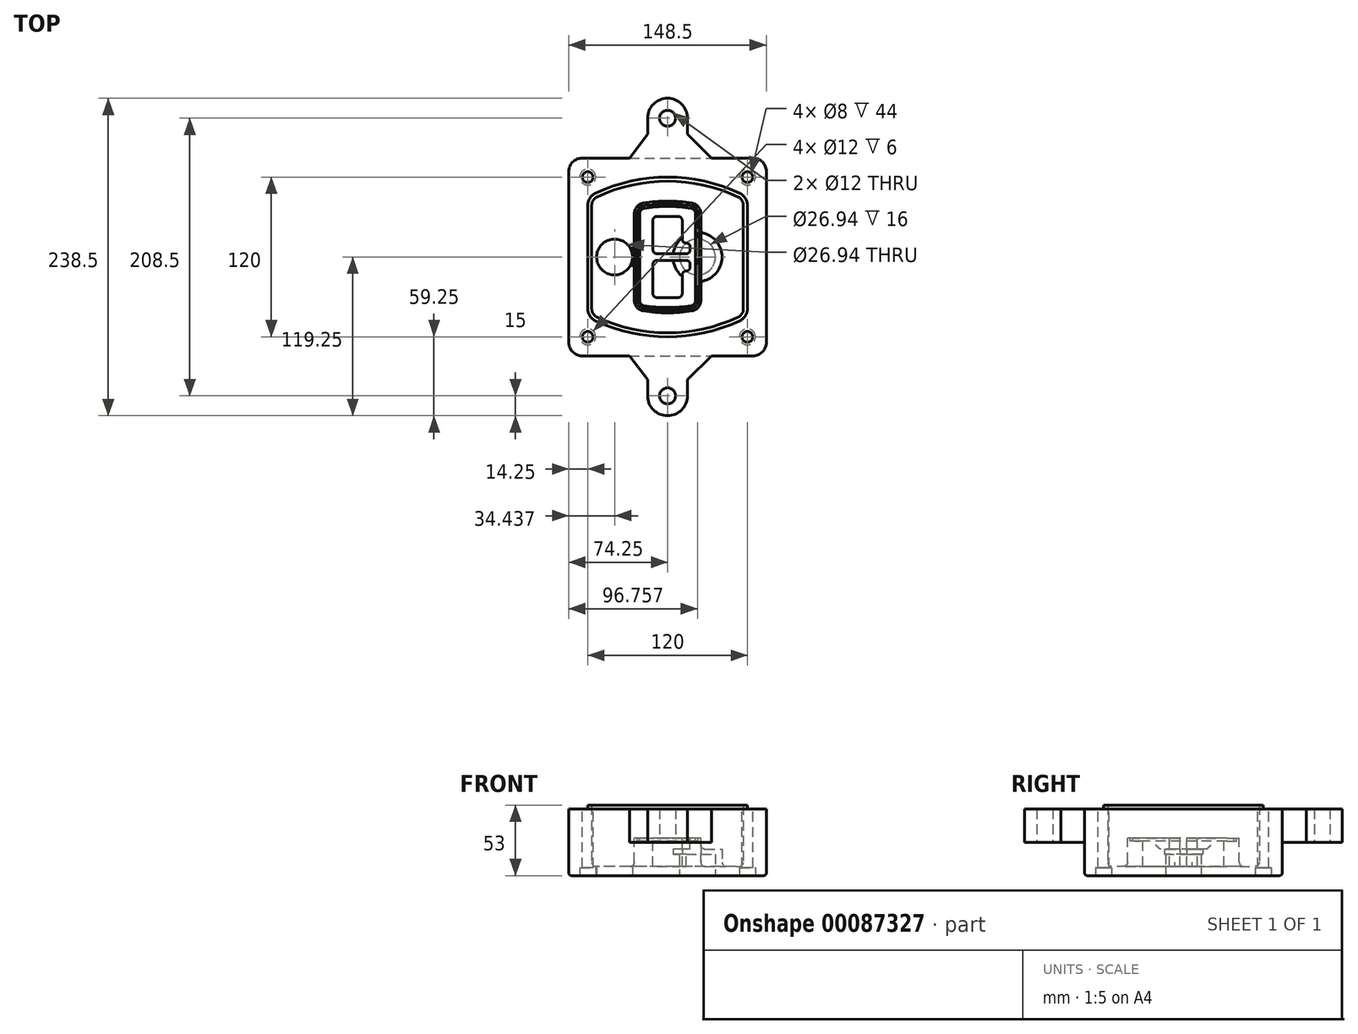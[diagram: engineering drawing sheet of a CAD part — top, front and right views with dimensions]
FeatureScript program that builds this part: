
annotation { "Feature Type Name" : "Feature", "Feature Type Description" : "" }
export const myFeature = defineFeature(function(context is Context, id is Id, definition is map)
    precondition{}
    {
        {
            var Q0;
            Q0=qCreatedBy(makeId("Top.planeOp"),FACE);
            var sketch = newSketch(context, id + "F0", { "sketchPlane" : qUnion([Q0])});
            skPoint(sketch, "E0.rect.middle", {"position": v(0, 0) * mm});
            skLineSegment(sketch, "E1.bottom", {"start": v(-64.25, -74.25) * mm, "end": v(64.25, -74.25) * mm});
            skLineSegment(sketch, "E1.top", {"start": v(-64.25, 74.25) * mm, "end": v(64.25, 74.25) * mm});
            skLineSegment(sketch, "E1.left", {"start": v(-74.25, -64.25) * mm, "end": v(-74.25, 64.25) * mm});
            skLineSegment(sketch, "E1.right", {"start": v(74.25, -64.25) * mm, "end": v(74.25, 64.25) * mm});
            skLineSegment(sketch, "E2", {"start": v(-74.25, 74.25) * mm, "end": v(74.25, -74.25) * mm, "construction": true});
            skLineSegment(sketch, "E3", {"start": v(74.25, 74.25) * mm, "end": v(-74.25, -74.25) * mm, "construction": true});
            skCircle(sketch, "E4", {"center": v(-60, 60) * mm, "radius": 4 * mm});
            skCircle(sketch, "E5", {"center": v(60, 60) * mm, "radius": 4 * mm});
            skCircle(sketch, "E6", {"center": v(60, -60) * mm, "radius": 4 * mm});
            skCircle(sketch, "E7", {"center": v(-60, -60) * mm, "radius": 4 * mm});
            skLineSegment(sketch, "E8", {"start": v(-60, 60) * mm, "end": v(60, 60) * mm, "construction": true});
            skLineSegment(sketch, "E9", {"start": v(60, 60) * mm, "end": v(60, -60) * mm, "construction": true});
            skLineSegment(sketch, "E10", {"start": v(60, -60) * mm, "end": v(-60, -60) * mm, "construction": true});
            skLineSegment(sketch, "E11", {"start": v(-60, -60) * mm, "end": v(-60, 60) * mm, "construction": true});
            skLineSegment(sketch, "E12", {"start": v(-60, 38.83) * mm, "end": v(-60, -38.83) * mm});
            skLineSegment(sketch, "E13", {"start": v(60, 38.83) * mm, "end": v(60, -38.83) * mm});
            skArc(sketch, "E14", {"start": v(54.26, 47.88) * mm, "mid": v(0, 60) * mm, "end": v(-54.26, 47.88) * mm});
            skArc(sketch, "E15", {"start": v(-54.26, -47.88) * mm, "mid": v(0, -60) * mm, "end": v(54.26, -47.88) * mm});
            skLineSegment(sketch, "E16", {"start": v(-60, 0) * mm, "end": v(60, 0) * mm, "construction": true});
            skPoint(sketch, "E17.visualSharp", {"position": v(-60, -45) * mm});
            skArc(sketch, "E17.filletArc", {"start": v(-60, -38.83) * mm, "mid": v(-58.44, -44.2) * mm, "end": v(-54.26, -47.88) * mm});
            skPoint(sketch, "E18.visualSharp", {"position": v(-60, 45) * mm});
            skArc(sketch, "E18.filletArc", {"start": v(-54.26, 47.88) * mm, "mid": v(-58.44, 44.2) * mm, "end": v(-60, 38.83) * mm});
            skPoint(sketch, "E19.visualSharp", {"position": v(60, 45) * mm});
            skArc(sketch, "E19.filletArc", {"start": v(60, 38.83) * mm, "mid": v(58.44, 44.2) * mm, "end": v(54.26, 47.88) * mm});
            skPoint(sketch, "E20.visualSharp", {"position": v(60, -45) * mm});
            skArc(sketch, "E20.filletArc", {"start": v(54.26, -47.88) * mm, "mid": v(58.44, -44.2) * mm, "end": v(60, -38.83) * mm});
            skPoint(sketch, "E21.visualSharp", {"position": v(-74.25, 74.25) * mm});
            skArc(sketch, "E21.filletArc", {"start": v(-64.25, 74.25) * mm, "mid": v(-71.32, 71.32) * mm, "end": v(-74.25, 64.25) * mm});
            skPoint(sketch, "E22.visualSharp", {"position": v(74.25, 74.25) * mm});
            skArc(sketch, "E22.filletArc", {"start": v(74.25, 64.25) * mm, "mid": v(71.32, 71.32) * mm, "end": v(64.25, 74.25) * mm});
            skPoint(sketch, "E23.visualSharp", {"position": v(74.25, -74.25) * mm});
            skArc(sketch, "E23.filletArc", {"start": v(64.25, -74.25) * mm, "mid": v(71.32, -71.32) * mm, "end": v(74.25, -64.25) * mm});
            skPoint(sketch, "E24.visualSharp", {"position": v(-74.25, -74.25) * mm});
            skArc(sketch, "E24.filletArc", {"start": v(-74.25, -64.25) * mm, "mid": v(-71.32, -71.32) * mm, "end": v(-64.25, -74.25) * mm});
            skArc(sketch, "E25.0", {"start": v(57, 38.83) * mm, "mid": v(55.9, 42.58) * mm, "end": v(52.98, 45.17) * mm});
            skLineSegment(sketch, "E25.1", {"start": v(57, 38.83) * mm, "end": v(57, -38.83) * mm});
            skArc(sketch, "E25.2", {"start": v(52.98, -45.17) * mm, "mid": v(55.9, -42.58) * mm, "end": v(57, -38.83) * mm});
            skArc(sketch, "E25.3", {"start": v(-52.98, -45.17) * mm, "mid": v(0, -57) * mm, "end": v(52.98, -45.17) * mm});
            skArc(sketch, "E25.4", {"start": v(-57, -38.83) * mm, "mid": v(-55.9, -42.58) * mm, "end": v(-52.98, -45.17) * mm});
            skArc(sketch, "E25.5", {"start": v(52.98, 45.17) * mm, "mid": v(0, 57) * mm, "end": v(-52.98, 45.17) * mm});
            skLineSegment(sketch, "E25.6", {"start": v(-57, 38.83) * mm, "end": v(-57, -38.83) * mm});
            skArc(sketch, "E25.7", {"start": v(-52.98, 45.17) * mm, "mid": v(-55.9, 42.58) * mm, "end": v(-57, 38.83) * mm});
            skArc(sketch, "E26.0", {"start": v(-55.96, 51.5) * mm, "mid": v(-61.82, 46.33) * mm, "end": v(-64, 38.83) * mm});
            skArc(sketch, "E26.1", {"start": v(55.96, 51.5) * mm, "mid": v(0, 64) * mm, "end": v(-55.96, 51.5) * mm});
            skArc(sketch, "E26.2", {"start": v(64, 38.83) * mm, "mid": v(61.82, 46.33) * mm, "end": v(55.96, 51.5) * mm});
            skLineSegment(sketch, "E26.3", {"start": v(64, 38.83) * mm, "end": v(64, -38.83) * mm});
            skArc(sketch, "E26.4", {"start": v(55.96, -51.5) * mm, "mid": v(61.82, -46.33) * mm, "end": v(64, -38.83) * mm});
            skLineSegment(sketch, "E26.5", {"start": v(-64, 38.83) * mm, "end": v(-64, -38.83) * mm});
            skArc(sketch, "E26.6", {"start": v(-55.96, -51.5) * mm, "mid": v(0, -64) * mm, "end": v(55.96, -51.5) * mm});
            skArc(sketch, "E26.7", {"start": v(-64, -38.83) * mm, "mid": v(-61.82, -46.33) * mm, "end": v(-55.96, -51.5) * mm});
            skSolve(sketch);
        }
        {
            var Q0;
            Q0=makeQuery(id+"F0.imprint","IMPRINT",FACE,{"disambiguationData":[TD([[makeQuery(id+"F0.imprint","IMPRINT",EDGE,{"derivedFrom":sQuery(id+"F0.wireOp",EDGE,"E1.bottom")}),1.0]])]});
            var Q1;
            Q1=makeQuery(id+"F0.imprint","IMPRINT",FACE,{"disambiguationData":[TD([[makeQuery(id+"F0.imprint","IMPRINT",EDGE,{"derivedFrom":sQuery(id+"F0.wireOp",EDGE,"E12")}),1.0]])]});
            var Q2;
            Q2=makeQuery(id+"F0.imprint","IMPRINT",FACE,{"disambiguationData":[TD([[makeQuery(id+"F0.imprint","IMPRINT",EDGE,{"derivedFrom":sQuery(id+"F0.wireOp",EDGE,"E25.0")}),1.0]])]});
            var Q3;
            Q3=makeQuery(id+"F0.imprint","IMPRINT",FACE,{"disambiguationData":[TD([[makeQuery(id+"F0.imprint","IMPRINT",EDGE,{"derivedFrom":sQuery(id+"F0.wireOp",EDGE,"E12")}),-1.0]])]});
            extrude(context, id + "F1", {"entities" : qUnion([Q0, Q1, Q2, Q3]), "oppositeDirection" : true, "depth" : 25 * mm});
        }
        {
            var Q0;
            Q0=makeQuery(id+"F0.imprint","IMPRINT",FACE,{"disambiguationData":[TD([[makeQuery(id+"F0.imprint","IMPRINT",EDGE,{"derivedFrom":sQuery(id+"F0.wireOp",EDGE,"E12")}),1.0]])]});
            extrude(context, id + "F2", {"entities" : qUnion([Q0]), "operationType" : NewBodyOperationType.ADD, "depth" : 3 * mm});
        }
        {
            var Q0;
            Q0=makeQuery(id+"F0.imprint","IMPRINT",FACE,{"disambiguationData":[TD([[makeQuery(id+"F0.imprint","IMPRINT",EDGE,{"derivedFrom":sQuery(id+"F0.wireOp",EDGE,"E25.0")}),1.0]])]});
            extrude(context, id + "F3", {"entities" : qUnion([Q0]), "operationType" : NewBodyOperationType.REMOVE, "oppositeDirection" : true, "depth" : 18 * mm});
        }
        {
            var Q0;
            Q0=makeQuery(id+"F2.opExtrude","CAP_FACE",FACE,{"disambiguationData":[OSD([sQuery(id+"F0.wireOp",EDGE,"E12"),sQuery(id+"F0.wireOp",EDGE,"E13"),sQuery(id+"F0.wireOp",EDGE,"E14"),sQuery(id+"F0.wireOp",EDGE,"E15"),sQuery(id+"F0.wireOp",EDGE,"E17.filletArc"),sQuery(id+"F0.wireOp",EDGE,"E18.filletArc"),sQuery(id+"F0.wireOp",EDGE,"E19.filletArc"),sQuery(id+"F0.wireOp",EDGE,"E20.filletArc"),sQuery(id+"F0.wireOp",EDGE,"E25.0"),sQuery(id+"F0.wireOp",EDGE,"E25.1"),sQuery(id+"F0.wireOp",EDGE,"E25.2"),sQuery(id+"F0.wireOp",EDGE,"E25.3"),sQuery(id+"F0.wireOp",EDGE,"E25.4"),sQuery(id+"F0.wireOp",EDGE,"E25.5"),sQuery(id+"F0.wireOp",EDGE,"E25.6"),sQuery(id+"F0.wireOp",EDGE,"E25.7")])],"isStart":false});
            var sketch = newSketch(context, id + "F4", { "sketchPlane" : qUnion([Q0])});
            skArc(sketch, "E27.0", {"start": v(-18.34, -40.45) * mm, "mid": v(0, -42) * mm, "end": v(18.34, -40.45) * mm});
            skArc(sketch, "E28.0", {"start": v(18.34, 40.45) * mm, "mid": v(0, 42) * mm, "end": v(-18.34, 40.45) * mm});
            skLineSegment(sketch, "E29", {"start": v(-25, 32.57) * mm, "end": v(-25, -32.57) * mm});
            skLineSegment(sketch, "E30", {"start": v(25, 32.57) * mm, "end": v(25, -32.57) * mm});
            skLineSegment(sketch, "E31", {"start": v(-25, 39.1) * mm, "end": v(25, 39.1) * mm, "construction": true});
            skLineSegment(sketch, "E32", {"start": v(-25, -39.1) * mm, "end": v(25, -39.1) * mm, "construction": true});
            skPoint(sketch, "E33.visualSharp", {"position": v(-25, 39.1) * mm});
            skArc(sketch, "E33.filletArc", {"start": v(-18.34, 40.45) * mm, "mid": v(-23.11, 37.73) * mm, "end": v(-25, 32.57) * mm});
            skPoint(sketch, "E34.visualSharp", {"position": v(25, 39.1) * mm});
            skArc(sketch, "E34.filletArc", {"start": v(25, 32.57) * mm, "mid": v(23.11, 37.73) * mm, "end": v(18.34, 40.45) * mm});
            skPoint(sketch, "E35.visualSharp", {"position": v(25, -39.1) * mm});
            skArc(sketch, "E35.filletArc", {"start": v(18.34, -40.45) * mm, "mid": v(23.11, -37.73) * mm, "end": v(25, -32.57) * mm});
            skPoint(sketch, "E36.visualSharp", {"position": v(-25, -39.1) * mm});
            skArc(sketch, "E36.filletArc", {"start": v(-25, -32.57) * mm, "mid": v(-23.11, -37.73) * mm, "end": v(-18.34, -40.45) * mm});
            skArc(sketch, "E37.0", {"start": v(52.98, 45.17) * mm, "mid": v(0, 57) * mm, "end": v(-52.98, 45.17) * mm});
            skArc(sketch, "E37.1", {"start": v(-52.98, 45.17) * mm, "mid": v(-55.9, 42.58) * mm, "end": v(-57, 38.83) * mm});
            skLineSegment(sketch, "E37.2", {"start": v(-57, 38.83) * mm, "end": v(-57, -38.83) * mm});
            skArc(sketch, "E37.3", {"start": v(-57, -38.83) * mm, "mid": v(-55.9, -42.58) * mm, "end": v(-52.98, -45.17) * mm});
            skArc(sketch, "E37.4", {"start": v(-52.98, -45.17) * mm, "mid": v(0, -57) * mm, "end": v(52.98, -45.17) * mm});
            skArc(sketch, "E37.5", {"start": v(52.98, -45.17) * mm, "mid": v(55.9, -42.58) * mm, "end": v(57, -38.83) * mm});
            skLineSegment(sketch, "E37.6", {"start": v(57, 38.83) * mm, "end": v(57, -38.83) * mm});
            skArc(sketch, "E37.7", {"start": v(57, 38.83) * mm, "mid": v(55.9, 42.58) * mm, "end": v(52.98, 45.17) * mm});
            skLineSegment(sketch, "E38.0", {"start": v(23, 32.57) * mm, "end": v(23, -32.57) * mm});
            skArc(sketch, "E38.1", {"start": v(18, -38.48) * mm, "mid": v(21.58, -36.44) * mm, "end": v(23, -32.57) * mm});
            skArc(sketch, "E38.2", {"start": v(-18, -38.48) * mm, "mid": v(0, -40) * mm, "end": v(18, -38.48) * mm});
            skArc(sketch, "E38.3", {"start": v(-23, -32.57) * mm, "mid": v(-21.58, -36.44) * mm, "end": v(-18, -38.48) * mm});
            skLineSegment(sketch, "E38.4", {"start": v(-23, 32.57) * mm, "end": v(-23, -32.57) * mm});
            skArc(sketch, "E38.5", {"start": v(23, 32.57) * mm, "mid": v(21.58, 36.44) * mm, "end": v(18, 38.48) * mm});
            skArc(sketch, "E38.6", {"start": v(-18, 38.48) * mm, "mid": v(-21.58, 36.44) * mm, "end": v(-23, 32.57) * mm});
            skArc(sketch, "E38.7", {"start": v(18, 38.48) * mm, "mid": v(0, 40) * mm, "end": v(-18, 38.48) * mm});
            skArc(sketch, "E39.0", {"start": v(21, 32.57) * mm, "mid": v(20.06, 35.15) * mm, "end": v(17.67, 36.5) * mm});
            skLineSegment(sketch, "E39.1", {"start": v(21, 32.57) * mm, "end": v(21, -32.57) * mm});
            skArc(sketch, "E39.2", {"start": v(17.67, -36.5) * mm, "mid": v(20.06, -35.15) * mm, "end": v(21, -32.57) * mm});
            skArc(sketch, "E39.3", {"start": v(-17.67, -36.5) * mm, "mid": v(0, -38) * mm, "end": v(17.67, -36.5) * mm});
            skArc(sketch, "E39.4", {"start": v(-21, -32.57) * mm, "mid": v(-20.06, -35.15) * mm, "end": v(-17.67, -36.5) * mm});
            skArc(sketch, "E39.5", {"start": v(17.67, 36.5) * mm, "mid": v(0, 38) * mm, "end": v(-17.67, 36.5) * mm});
            skLineSegment(sketch, "E39.6", {"start": v(-21, 32.57) * mm, "end": v(-21, -32.57) * mm});
            skArc(sketch, "E39.7", {"start": v(-17.67, 36.5) * mm, "mid": v(-20.06, 35.15) * mm, "end": v(-21, 32.57) * mm});
            skLineSegment(sketch, "E40", {"start": v(-25, 0) * mm, "end": v(25, 0) * mm, "construction": true});
            skLineSegment(sketch, "E41", {"start": v(-11, 5.5) * mm, "end": v(-11, 27.5) * mm});
            skLineSegment(sketch, "E42", {"start": v(-8, 30.5) * mm, "end": v(8, 30.5) * mm});
            skLineSegment(sketch, "E43", {"start": v(11, 27.5) * mm, "end": v(11, 13.5) * mm});
            skLineSegment(sketch, "E44", {"start": v(14, 10.5) * mm, "end": v(14, 10.5) * mm});
            skLineSegment(sketch, "E45", {"start": v(17, 7.5) * mm, "end": v(17, 5.5) * mm});
            skLineSegment(sketch, "E46", {"start": v(14, 2.5) * mm, "end": v(-8, 2.5) * mm});
            skPoint(sketch, "E47.visualSharp", {"position": v(-11, 30.5) * mm});
            skArc(sketch, "E47.filletArc", {"start": v(-8, 30.5) * mm, "mid": v(-10.12, 29.62) * mm, "end": v(-11, 27.5) * mm});
            skPoint(sketch, "E48.visualSharp", {"position": v(11, 30.5) * mm});
            skArc(sketch, "E48.filletArc", {"start": v(11, 27.5) * mm, "mid": v(10.12, 29.62) * mm, "end": v(8, 30.5) * mm});
            skPoint(sketch, "E49.visualSharp", {"position": v(11, 10.5) * mm});
            skArc(sketch, "E49.filletArc", {"start": v(11, 13.5) * mm, "mid": v(11.88, 11.38) * mm, "end": v(14, 10.5) * mm});
            skPoint(sketch, "E50.visualSharp", {"position": v(17, 10.5) * mm});
            skArc(sketch, "E50.filletArc", {"start": v(17, 7.5) * mm, "mid": v(16.12, 9.62) * mm, "end": v(14, 10.5) * mm});
            skPoint(sketch, "E51.visualSharp", {"position": v(17, 2.5) * mm});
            skArc(sketch, "E51.filletArc", {"start": v(14, 2.5) * mm, "mid": v(16.12, 3.38) * mm, "end": v(17, 5.5) * mm});
            skPoint(sketch, "E52.visualSharp", {"position": v(-11, 2.5) * mm});
            skArc(sketch, "E52.filletArc", {"start": v(-11, 5.5) * mm, "mid": v(-10.12, 3.38) * mm, "end": v(-8, 2.5) * mm});
            skLineSegment(sketch, "E53.0.MirrorCS", {"start": v(14, -2.5) * mm, "end": v(-8, -2.5) * mm});
            skArc(sketch, "E54.0.MirrorCS", {"start": v(-11, -5.5) * mm, "mid": v(-10.12, -3.38) * mm, "end": v(-8, -2.5) * mm});
            skLineSegment(sketch, "E55.0.MirrorCS", {"start": v(-11, -5.5) * mm, "end": v(-11, -27.5) * mm});
            skArc(sketch, "E56.0.MirrorCS", {"start": v(-8, -30.5) * mm, "mid": v(-10.12, -29.62) * mm, "end": v(-11, -27.5) * mm});
            skLineSegment(sketch, "E57.0.MirrorCS", {"start": v(-8, -30.5) * mm, "end": v(8, -30.5) * mm});
            skArc(sketch, "E58.0.MirrorCS", {"start": v(11, -27.5) * mm, "mid": v(10.12, -29.62) * mm, "end": v(8, -30.5) * mm});
            skLineSegment(sketch, "E59.0.MirrorCS", {"start": v(11, -27.5) * mm, "end": v(11, -13.5) * mm});
            skArc(sketch, "E60.0.MirrorCS", {"start": v(11, -13.5) * mm, "mid": v(11.88, -11.38) * mm, "end": v(14, -10.5) * mm});
            skArc(sketch, "E61.0.MirrorCS", {"start": v(17, -7.5) * mm, "mid": v(16.12, -9.62) * mm, "end": v(14, -10.5) * mm});
            skLineSegment(sketch, "E62.0.MirrorCS", {"start": v(17, -7.5) * mm, "end": v(17, -5.5) * mm});
            skArc(sketch, "E63.0.MirrorCS", {"start": v(14, -2.5) * mm, "mid": v(16.12, -3.38) * mm, "end": v(17, -5.5) * mm});
            skSolve(sketch);
        }
        {
            var Q0;
            Q0=makeQuery(id+"F4.imprint","IMPRINT",FACE,{"disambiguationData":[TD([[makeQuery(id+"F4.imprint","IMPRINT",EDGE,{"derivedFrom":sQuery(id+"F4.wireOp",EDGE,"E27.0")}),1.0]])]});
            var Q1;
            Q1=makeQuery(id+"F4.imprint","IMPRINT",FACE,{"disambiguationData":[TD([[makeQuery(id+"F4.imprint","IMPRINT",EDGE,{"derivedFrom":sQuery(id+"F4.wireOp",EDGE,"E38.0")}),-1.0]])]});
            var Q2;
            Q2=makeQuery(id+"F4.imprint","IMPRINT",FACE,{"disambiguationData":[TD([[makeQuery(id+"F4.imprint","IMPRINT",EDGE,{"derivedFrom":sQuery(id+"F4.wireOp",EDGE,"E39.0")}),1.0]])]});
            extrude(context, id + "F5", {"entities" : qUnion([Q0, Q1, Q2]), "operationType" : NewBodyOperationType.ADD, "endBound" : BoundingType.UP_TO_NEXT, "oppositeDirection" : true, "depth" : 25 * mm});
        }
        {
            var Q0;
            Q0=makeQuery(id+"F4.imprint","IMPRINT",FACE,{"disambiguationData":[TD([[makeQuery(id+"F4.imprint","IMPRINT",EDGE,{"derivedFrom":sQuery(id+"F4.wireOp",EDGE,"E38.0")}),-1.0]])]});
            extrude(context, id + "F6", {"entities" : qUnion([Q0]), "operationType" : NewBodyOperationType.REMOVE, "oppositeDirection" : true, "depth" : 2 * mm});
        }
        {
            var Q0;
            Q0=makeQuery(id+"F1.opExtrude","CAP_FACE",FACE,{"disambiguationData":[OSD([sQuery(id+"F0.wireOp",EDGE,"E1.bottom"),sQuery(id+"F0.wireOp",EDGE,"E1.top"),sQuery(id+"F0.wireOp",EDGE,"E1.left"),sQuery(id+"F0.wireOp",EDGE,"E1.right"),sQuery(id+"F0.wireOp",EDGE,"E4"),sQuery(id+"F0.wireOp",EDGE,"E5"),sQuery(id+"F0.wireOp",EDGE,"E6"),sQuery(id+"F0.wireOp",EDGE,"E7"),sQuery(id+"F0.wireOp",EDGE,"E21.filletArc"),sQuery(id+"F0.wireOp",EDGE,"E22.filletArc"),sQuery(id+"F0.wireOp",EDGE,"E23.filletArc"),sQuery(id+"F0.wireOp",EDGE,"E24.filletArc")])],"isStart":false});
            var sketch = newSketch(context, id + "F7", { "sketchPlane" : qUnion([Q0])});
            skCircle(sketch, "E64", {"center": v(22.5, 0) * mm, "radius": 13.47 * mm});
            skCircle(sketch, "E65", {"center": v(-39.81, 0) * mm, "radius": 13.47 * mm});
            skLineSegment(sketch, "E66", {"start": v(74.25, 0) * mm, "end": v(-74.25, 0) * mm});
            skCircle(sketch, "E67", {"center": v(22.5, 0) * mm, "radius": 18.47 * mm});
            skCircle(sketch, "E68", {"center": v(60, -60) * mm, "radius": 6 * mm});
            skCircle(sketch, "E69", {"center": v(-60, -60) * mm, "radius": 6 * mm});
            skCircle(sketch, "E70", {"center": v(-60, 60) * mm, "radius": 6 * mm});
            skCircle(sketch, "E71", {"center": v(60, 60) * mm, "radius": 6 * mm});
            skSolve(sketch);
        }
        {
            var Q0;
            {var subQ1=sQuery(id+"F7.wireOp",EDGE,"E66");var subQ4=sQuery(id+"F7.wireOp",EDGE,"E64");var subQ6=makeQuery(id+"F7.imprint","INTERSECT",VERTEX,{"disambiguationData":[OD(0.0)],"derivedFrom":[subQ4,subQ1]});Q0=makeQuery(id+"F7.imprint","IMPRINT",FACE,{"disambiguationData":[TD([[makeQuery(id+"F7.imprint","IMPRINT",EDGE,{"disambiguationData":[TD([[subQ6,-1.0]])],"derivedFrom":subQ4}),-1.0]])]});}
            var Q1;
            {var subQ0=sQuery(id+"F7.wireOp",EDGE,"E66");var subQ1=sQuery(id+"F7.wireOp",EDGE,"E64");var subQ3=makeQuery(id+"F7.imprint","INTERSECT",VERTEX,{"disambiguationData":[OD(0.0)],"derivedFrom":[subQ1,subQ0]});Q1=makeQuery(id+"F7.imprint","IMPRINT",FACE,{"disambiguationData":[TD([[makeQuery(id+"F7.imprint","IMPRINT",EDGE,{"disambiguationData":[TD([[subQ3,-1.0]])],"derivedFrom":subQ1}),1.0]])]});}
            var Q2;
            {var subQ0=sQuery(id+"F7.wireOp",EDGE,"E66");var subQ1=sQuery(id+"F7.wireOp",EDGE,"E64");var subQ3=makeQuery(id+"F7.imprint","INTERSECT",VERTEX,{"disambiguationData":[OD(0.0)],"derivedFrom":[subQ1,subQ0]});Q2=makeQuery(id+"F7.imprint","IMPRINT",FACE,{"disambiguationData":[TD([[makeQuery(id+"F7.imprint","IMPRINT",EDGE,{"disambiguationData":[TD([[subQ3,1.0]])],"derivedFrom":subQ1}),1.0]])]});}
            var Q3;
            {var subQ1=sQuery(id+"F7.wireOp",EDGE,"E66");var subQ4=sQuery(id+"F7.wireOp",EDGE,"E64");var subQ6=makeQuery(id+"F7.imprint","INTERSECT",VERTEX,{"disambiguationData":[OD(0.0)],"derivedFrom":[subQ4,subQ1]});Q3=makeQuery(id+"F7.imprint","IMPRINT",FACE,{"disambiguationData":[TD([[makeQuery(id+"F7.imprint","IMPRINT",EDGE,{"disambiguationData":[TD([[subQ6,1.0]])],"derivedFrom":subQ4}),-1.0]])]});}
            extrude(context, id + "F8", {"entities" : qUnion([Q0, Q1, Q2, Q3]), "operationType" : NewBodyOperationType.ADD, "oppositeDirection" : true, "depth" : 20 * mm});
        }
        {
            var Q0;
            {var subQ0=sQuery(id+"F7.wireOp",EDGE,"E66");var subQ1=sQuery(id+"F7.wireOp",EDGE,"E64");var subQ3=makeQuery(id+"F7.imprint","INTERSECT",VERTEX,{"disambiguationData":[OD(0.0)],"derivedFrom":[subQ1,subQ0]});Q0=makeQuery(id+"F7.imprint","IMPRINT",FACE,{"disambiguationData":[TD([[makeQuery(id+"F7.imprint","IMPRINT",EDGE,{"disambiguationData":[TD([[subQ3,-1.0]])],"derivedFrom":subQ1}),1.0]])]});}
            var Q1;
            {var subQ0=sQuery(id+"F7.wireOp",EDGE,"E66");var subQ1=sQuery(id+"F7.wireOp",EDGE,"E64");var subQ3=makeQuery(id+"F7.imprint","INTERSECT",VERTEX,{"disambiguationData":[OD(0.0)],"derivedFrom":[subQ1,subQ0]});Q1=makeQuery(id+"F7.imprint","IMPRINT",FACE,{"disambiguationData":[TD([[makeQuery(id+"F7.imprint","IMPRINT",EDGE,{"disambiguationData":[TD([[subQ3,1.0]])],"derivedFrom":subQ1}),1.0]])]});}
            extrude(context, id + "F9", {"entities" : qUnion([Q0, Q1]), "operationType" : NewBodyOperationType.REMOVE, "oppositeDirection" : true, "depth" : 16 * mm});
        }
        {
            var Q0;
            {var subQ0=sQuery(id+"F7.wireOp",EDGE,"E66");var subQ1=sQuery(id+"F7.wireOp",EDGE,"E65");var subQ3=makeQuery(id+"F7.imprint","INTERSECT",VERTEX,{"disambiguationData":[OD(0.0)],"derivedFrom":[subQ1,subQ0]});Q0=makeQuery(id+"F7.imprint","IMPRINT",FACE,{"disambiguationData":[TD([[makeQuery(id+"F7.imprint","IMPRINT",EDGE,{"disambiguationData":[TD([[subQ3,-1.0]])],"derivedFrom":subQ1}),1.0]])]});}
            var Q1;
            {var subQ0=sQuery(id+"F7.wireOp",EDGE,"E66");var subQ1=sQuery(id+"F7.wireOp",EDGE,"E65");var subQ3=makeQuery(id+"F7.imprint","INTERSECT",VERTEX,{"disambiguationData":[OD(0.0)],"derivedFrom":[subQ1,subQ0]});Q1=makeQuery(id+"F7.imprint","IMPRINT",FACE,{"disambiguationData":[TD([[makeQuery(id+"F7.imprint","IMPRINT",EDGE,{"disambiguationData":[TD([[subQ3,1.0]])],"derivedFrom":subQ1}),1.0]])]});}
            extrude(context, id + "F10", {"entities" : qUnion([Q0, Q1]), "operationType" : NewBodyOperationType.REMOVE, "oppositeDirection" : true, "depth" : 25 * mm});
        }
        {
            var Q0;
            Q0=makeQuery(id+"F7.imprint","IMPRINT",FACE,{"disambiguationData":[TD([[makeQuery(id+"F7.imprint","IMPRINT",EDGE,{"derivedFrom":sQuery(id+"F7.wireOp",EDGE,"E68")}),1.0]])]});
            var Q1;
            Q1=makeQuery(id+"F7.imprint","IMPRINT",FACE,{"disambiguationData":[TD([[makeQuery(id+"F7.imprint","IMPRINT",EDGE,{"derivedFrom":makeQuery(id+"F1.opExtrude","CAP_EDGE",EDGE,{"disambiguationData":[OSD([sQuery(id+"F0.wireOp",EDGE,"E5")])],"isStart":false})}),-1.0]])]});
            var Q2;
            Q2=makeQuery(id+"F7.imprint","IMPRINT",FACE,{"disambiguationData":[TD([[makeQuery(id+"F7.imprint","IMPRINT",EDGE,{"derivedFrom":sQuery(id+"F7.wireOp",EDGE,"E69")}),1.0]])]});
            var Q3;
            Q3=makeQuery(id+"F7.imprint","IMPRINT",FACE,{"disambiguationData":[TD([[makeQuery(id+"F7.imprint","IMPRINT",EDGE,{"derivedFrom":makeQuery(id+"F1.opExtrude","CAP_EDGE",EDGE,{"disambiguationData":[OSD([sQuery(id+"F0.wireOp",EDGE,"E4")])],"isStart":false})}),-1.0]])]});
            var Q4;
            Q4=makeQuery(id+"F7.imprint","IMPRINT",FACE,{"disambiguationData":[TD([[makeQuery(id+"F7.imprint","IMPRINT",EDGE,{"derivedFrom":sQuery(id+"F7.wireOp",EDGE,"E70")}),1.0]])]});
            var Q5;
            Q5=makeQuery(id+"F7.imprint","IMPRINT",FACE,{"disambiguationData":[TD([[makeQuery(id+"F7.imprint","IMPRINT",EDGE,{"derivedFrom":makeQuery(id+"F1.opExtrude","CAP_EDGE",EDGE,{"disambiguationData":[OSD([sQuery(id+"F0.wireOp",EDGE,"E7")])],"isStart":false})}),-1.0]])]});
            var Q6;
            Q6=makeQuery(id+"F7.imprint","IMPRINT",FACE,{"disambiguationData":[TD([[makeQuery(id+"F7.imprint","IMPRINT",EDGE,{"derivedFrom":sQuery(id+"F7.wireOp",EDGE,"E71")}),1.0]])]});
            var Q7;
            Q7=makeQuery(id+"F7.imprint","IMPRINT",FACE,{"disambiguationData":[TD([[makeQuery(id+"F7.imprint","IMPRINT",EDGE,{"derivedFrom":makeQuery(id+"F1.opExtrude","CAP_EDGE",EDGE,{"disambiguationData":[OSD([sQuery(id+"F0.wireOp",EDGE,"E6")])],"isStart":false})}),-1.0]])]});
            extrude(context, id + "F11", {"entities" : qUnion([Q0, Q1, Q2, Q3, Q4, Q5, Q6, Q7]), "operationType" : NewBodyOperationType.REMOVE, "oppositeDirection" : true, "depth" : 6 * mm});
        }
        {
            var Q0;
            Q0=makeQuery(id+"F9.boolean.opBoolean","COPY",FACE,{"derivedFrom":makeQuery(id+"F9.opExtrude","CAP_FACE",FACE,{"disambiguationData":[OSD([sQuery(id+"F7.wireOp",EDGE,"E64")])],"isStart":false})});
            var sketch = newSketch(context, id + "F12", { "sketchPlane" : qUnion([Q0])});
            skArc(sketch, "E72.0", {"start": v(11, 14.45) * mm, "mid": v(6.45, 9.13) * mm, "end": v(4.2, 2.5) * mm});
            skArc(sketch, "E72.1", {"start": v(4.2, -2.5) * mm, "mid": v(6.45, -9.13) * mm, "end": v(11, -14.45) * mm});
            skLineSegment(sketch, "E73", {"start": v(4.2, -2.5) * mm, "end": v(14, -2.5) * mm});
            skLineSegment(sketch, "E74.0", {"start": v(14, 2.5) * mm, "end": v(4.2, 2.5) * mm});
            skArc(sketch, "E74.1", {"start": v(14, 2.5) * mm, "mid": v(16.12, 3.38) * mm, "end": v(17, 5.5) * mm});
            skLineSegment(sketch, "E74.2", {"start": v(17, 7.5) * mm, "end": v(17, 5.5) * mm});
            skArc(sketch, "E74.3", {"start": v(17, 7.5) * mm, "mid": v(16.12, 9.62) * mm, "end": v(14, 10.5) * mm});
            skArc(sketch, "E74.4", {"start": v(11, 13.5) * mm, "mid": v(11.88, 11.38) * mm, "end": v(14, 10.5) * mm});
            skLineSegment(sketch, "E74.5", {"start": v(11, 14.45) * mm, "end": v(11, 13.5) * mm});
            skLineSegment(sketch, "E74.7", {"start": v(14, -2.5) * mm, "end": v(4.2, -2.5) * mm});
            skArc(sketch, "E74.8", {"start": v(14, -2.5) * mm, "mid": v(16.12, -3.38) * mm, "end": v(17, -5.5) * mm});
            skLineSegment(sketch, "E74.9", {"start": v(17, -7.5) * mm, "end": v(17, -5.5) * mm});
            skArc(sketch, "E74.10", {"start": v(17, -7.5) * mm, "mid": v(16.12, -9.62) * mm, "end": v(14, -10.5) * mm});
            skArc(sketch, "E74.11", {"start": v(11, -13.5) * mm, "mid": v(11.88, -11.38) * mm, "end": v(14, -10.5) * mm});
            skLineSegment(sketch, "E74.12", {"start": v(11, -14.45) * mm, "end": v(11, -13.5) * mm});
            skPoint(sketch, "E75.orphan", {"position": v(11, -27.5) * mm});
            skPoint(sketch, "E76.orphan", {"position": v(-8, -2.5) * mm});
            skPoint(sketch, "E77.orphan", {"position": v(-8, 2.5) * mm});
            skPoint(sketch, "E78.orphan", {"position": v(11, 27.5) * mm});
            skSolve(sketch);
        }
        {
            var Q0;
            {var subQ7=sQuery(id+"F12.wireOp",EDGE,"E72.0");var subQ14=sQuery(id+"F12.wireOp",EDGE,"E72.1");var subQ16=sQuery(id+"F12.wireOp",EDGE,"E74.1");var subQ18=sQuery(id+"F12.wireOp",EDGE,"E74.8");Q0=qUnion([makeQuery(id+"F12.imprint","IMPRINT",FACE,{"disambiguationData":[TD([[makeQuery(id+"F12.imprint","IMPRINT",EDGE,{"derivedFrom":subQ7}),1.0]])]}),makeQuery(id+"F12.imprint","IMPRINT",FACE,{"disambiguationData":[TD([[makeQuery(id+"F12.imprint","IMPRINT",EDGE,{"derivedFrom":subQ14}),1.0]])]}),makeQuery(id+"F12.imprint","IMPRINT",FACE,{"disambiguationData":[TD([[makeQuery(id+"F12.imprint","IMPRINT",EDGE,{"derivedFrom":subQ16}),1.0]])]}),makeQuery(id+"F12.imprint","IMPRINT",FACE,{"disambiguationData":[TD([[makeQuery(id+"F12.imprint","IMPRINT",EDGE,{"derivedFrom":subQ18}),-1.0]])]})]);}
            var Q1;
            Q1=makeQuery(id+"F5.boolean.opBoolean","SPLIT",FACE,{"disambiguationData":[TD([makeQuery(id+"F5.opExtrude","SWEPT_FACE",FACE,{"disambiguationData":[OSD([sQuery(id+"F4.wireOp",EDGE,"E41")])]})])],"derivedFrom":makeQuery(id+"F3.boolean.opBoolean","COPY",FACE,{"derivedFrom":makeQuery(id+"F3.opExtrude","CAP_FACE",FACE,{"disambiguationData":[OSD([sQuery(id+"F0.wireOp",EDGE,"E25.0"),sQuery(id+"F0.wireOp",EDGE,"E25.1"),sQuery(id+"F0.wireOp",EDGE,"E25.2"),sQuery(id+"F0.wireOp",EDGE,"E25.3"),sQuery(id+"F0.wireOp",EDGE,"E25.4"),sQuery(id+"F0.wireOp",EDGE,"E25.5"),sQuery(id+"F0.wireOp",EDGE,"E25.6"),sQuery(id+"F0.wireOp",EDGE,"E25.7")])],"isStart":false})})});
            extrude(context, id + "F13", {"entities" : qUnion([Q0]), "operationType" : NewBodyOperationType.REMOVE, "endBound" : BoundingType.UP_TO_SURFACE, "endBoundEntityFace" : qUnion([Q1]), "depth" : 25 * mm});
        }
        {
            var Q0;
            Q0=makeQuery(id+"F3.boolean.opBoolean","COPY",EDGE,{"derivedFrom":makeQuery(id+"F3.opExtrude","CAP_EDGE",EDGE,{"disambiguationData":[OSD([sQuery(id+"F0.wireOp",EDGE,"E25.6")])],"isStart":false})});
            var Q1;
            Q1=makeQuery(id+"F8.boolean.opBoolean","INTERSECT",EDGE,{"derivedFrom":[makeQuery(id+"F5.opExtrude","SWEPT_FACE",FACE,{"disambiguationData":[OSD([sQuery(id+"F4.wireOp",EDGE,"E30")])]}),makeQuery(id+"F8.opExtrude","CAP_FACE",FACE,{"disambiguationData":[OSD([sQuery(id+"F7.wireOp",EDGE,"E67")])],"isStart":false})]});
            var Q2;
            Q2=makeQuery(id+"F8.boolean.opBoolean","INTERSECT",EDGE,{"disambiguationData":[OD(1.0)],"derivedFrom":[makeQuery(id+"F5.opExtrude","SWEPT_FACE",FACE,{"disambiguationData":[OSD([sQuery(id+"F4.wireOp",EDGE,"E30")])]}),makeQuery(id+"F8.opExtrude","SWEPT_FACE",FACE,{"disambiguationData":[OSD([sQuery(id+"F7.wireOp",EDGE,"E67")])]})]});
            var Q3;
            {var subQ0=sQuery(id+"F4.wireOp",EDGE,"E30");Q3=makeQuery(id+"F8.boolean.opBoolean","SPLIT",EDGE,{"disambiguationData":[TD([makeQuery(id+"F5.opExtrude","SWEPT_FACE",FACE,{"disambiguationData":[OSD([sQuery(id+"F4.wireOp",EDGE,"E35.filletArc")])]})])],"derivedFrom":makeQuery(id+"F5.opExtrude","CAP_EDGE",EDGE,{"disambiguationData":[OSD([subQ0])],"isStart":false})});}
            var Q4;
            {var subQ0=sQuery(id+"F0.wireOp",EDGE,"E25.7");var subQ1=sQuery(id+"F0.wireOp",EDGE,"E25.1");var subQ2=sQuery(id+"F0.wireOp",EDGE,"E25.6");var subQ3=sQuery(id+"F0.wireOp",EDGE,"E25.5");var subQ4=sQuery(id+"F0.wireOp",EDGE,"E25.4");var subQ5=sQuery(id+"F0.wireOp",EDGE,"E25.0");var subQ6=sQuery(id+"F0.wireOp",EDGE,"E25.2");var subQ7=sQuery(id+"F0.wireOp",EDGE,"E25.3");Q4=makeQuery(id+"F8.boolean.opBoolean","INTERSECT",EDGE,{"derivedFrom":[makeQuery(id+"F5.boolean.opBoolean","SPLIT",FACE,{"disambiguationData":[TD([makeQuery(id+"F2.opExtrude","SWEPT_FACE",FACE,{"disambiguationData":[OSD([subQ5])]})])],"derivedFrom":makeQuery(id+"F3.boolean.opBoolean","COPY",FACE,{"derivedFrom":makeQuery(id+"F3.opExtrude","CAP_FACE",FACE,{"disambiguationData":[OSD([subQ5,subQ1,subQ6,subQ7,subQ4,subQ3,subQ2,subQ0])],"isStart":false})})}),makeQuery(id+"F8.opExtrude","SWEPT_FACE",FACE,{"disambiguationData":[OSD([sQuery(id+"F7.wireOp",EDGE,"E67")])]})]});}
            var Q5;
            Q5=makeQuery(id+"F8.boolean.opBoolean","INTERSECT",EDGE,{"disambiguationData":[OD(0.0)],"derivedFrom":[makeQuery(id+"F5.opExtrude","SWEPT_FACE",FACE,{"disambiguationData":[OSD([sQuery(id+"F4.wireOp",EDGE,"E30")])]}),makeQuery(id+"F8.opExtrude","SWEPT_FACE",FACE,{"disambiguationData":[OSD([sQuery(id+"F7.wireOp",EDGE,"E67")])]})]});
            fillet(context, id + "F14", {"entities" : qUnion([Q0, Q1, Q2, Q3, Q4, Q5]), "radius" : 3 * mm, "tangentPropagation" : true, "allowEdgeOverflow" : false});
        }
        {
            var Q0;
            Q0=makeQuery(id+"F1.opExtrude","CAP_EDGE",EDGE,{"disambiguationData":[OSD([sQuery(id+"F0.wireOp",EDGE,"E1.bottom")])],"isStart":false});
            fillet(context, id + "F15", {"entities" : qUnion([Q0]), "radius" : 2 * mm, "tangentPropagation" : true, "allowEdgeOverflow" : false});
        }
        {
            var Q0;
            {var subQ0=sQuery(id+"F0.wireOp",EDGE,"E22.filletArc");var subQ1=sQuery(id+"F0.wireOp",EDGE,"E7");var subQ2=sQuery(id+"F0.wireOp",EDGE,"E6");var subQ3=sQuery(id+"F0.wireOp",EDGE,"E5");var subQ4=sQuery(id+"F0.wireOp",EDGE,"E4");var subQ5=sQuery(id+"F0.wireOp",EDGE,"E1.bottom");var subQ6=sQuery(id+"F0.wireOp",EDGE,"E21.filletArc");var subQ7=sQuery(id+"F0.wireOp",EDGE,"E1.top");var subQ8=sQuery(id+"F0.wireOp",EDGE,"E1.left");var subQ9=sQuery(id+"F0.wireOp",EDGE,"E1.right");var subQ10=sQuery(id+"F0.wireOp",EDGE,"E23.filletArc");var subQ11=sQuery(id+"F0.wireOp",EDGE,"E24.filletArc");Q0=makeQuery(id+"F2.boolean.opBoolean","SPLIT",FACE,{"disambiguationData":[TD([makeQuery(id+"F1.opExtrude","SWEPT_FACE",FACE,{"disambiguationData":[OSD([subQ5])]})])],"derivedFrom":makeQuery(id+"F1.opExtrude","CAP_FACE",FACE,{"disambiguationData":[OSD([subQ5,subQ7,subQ8,subQ9,subQ4,subQ3,subQ2,subQ1,subQ6,subQ0,subQ10,subQ11])],"isStart":true})});}
            var sketch = newSketch(context, id + "F16", { "sketchPlane" : qUnion([Q0])});
            skLineSegment(sketch, "E79.0", {"start": v(-64.25, 74.25) * mm, "end": v(64.25, 74.25) * mm});
            skLineSegment(sketch, "E80", {"start": v(0, 74.25) * mm, "end": v(0, 104.25) * mm, "construction": true});
            skCircle(sketch, "E81", {"center": v(0, 104.25) * mm, "radius": 6 * mm});
            skArc(sketch, "E82", {"start": v(15, 104.25) * mm, "mid": v(0, 119.25) * mm, "end": v(-15, 104.25) * mm});
            skLineSegment(sketch, "E83", {"start": v(15, 104.25) * mm, "end": v(15, 92.25) * mm});
            skLineSegment(sketch, "E84", {"start": v(-15, 104.25) * mm, "end": v(-15, 92.25) * mm});
            skLineSegment(sketch, "E85", {"start": v(15, 92.25) * mm, "end": v(33, 74.25) * mm});
            skLineSegment(sketch, "E86", {"start": v(-15, 92.25) * mm, "end": v(-28.7, 74.25) * mm});
            skLineSegment(sketch, "E87", {"start": v(0, 0) * mm, "end": v(140.66, 0) * mm, "construction": true});
            skLineSegment(sketch, "E88.MirrorCS", {"start": v(-15, -92.25) * mm, "end": v(-28.7, -74.25) * mm});
            skLineSegment(sketch, "E89.MirrorCS", {"start": v(-15, -104.25) * mm, "end": v(-15, -92.25) * mm});
            skArc(sketch, "E90.MirrorCS", {"start": v(15, -104.25) * mm, "mid": v(0, -119.25) * mm, "end": v(-15, -104.25) * mm});
            skLineSegment(sketch, "E91.MirrorCS", {"start": v(15, -92.25) * mm, "end": v(33, -74.25) * mm});
            skLineSegment(sketch, "E92.MirrorCS", {"start": v(15, -104.25) * mm, "end": v(15, -92.25) * mm});
            skCircle(sketch, "E93.MirrorC", {"center": v(0, -104.25) * mm, "radius": 6 * mm});
            skSolve(sketch);
        }
        {
            var Q0;
            Q0=makeQuery(id+"F16.imprint","IMPRINT",FACE,{"disambiguationData":[TD([[makeQuery(id+"F16.imprint","IMPRINT",EDGE,{"derivedFrom":sQuery(id+"F16.wireOp",EDGE,"E81")}),-1.0]])]});
            var Q1;
            Q1=makeQuery(id+"F16.imprint","IMPRINT",FACE,{"disambiguationData":[TD([[makeQuery(id+"F16.imprint","IMPRINT",EDGE,{"derivedFrom":makeQuery(id+"F1.opExtrude","CAP_EDGE",EDGE,{"disambiguationData":[OSD([sQuery(id+"F0.wireOp",EDGE,"E1.left")])],"isStart":true})}),-1.0]])]});
            var Q2;
            {var subQ0=sQuery(id+"F16.wireOp",EDGE,"E88.MirrorCS");Q2=makeQuery(id+"F16.imprint","IMPRINT",FACE,{"disambiguationData":[TD([[makeQuery(id+"F16.imprint","IMPRINT",EDGE,{"derivedFrom":subQ0}),-1.0]])]});}
            var Q3;
            Q3=makeQuery(id+"F2.opExtrude","CAP_FACE",FACE,{"disambiguationData":[OSD([sQuery(id+"F0.wireOp",EDGE,"E12"),sQuery(id+"F0.wireOp",EDGE,"E13"),sQuery(id+"F0.wireOp",EDGE,"E14"),sQuery(id+"F0.wireOp",EDGE,"E15"),sQuery(id+"F0.wireOp",EDGE,"E17.filletArc"),sQuery(id+"F0.wireOp",EDGE,"E18.filletArc"),sQuery(id+"F0.wireOp",EDGE,"E19.filletArc"),sQuery(id+"F0.wireOp",EDGE,"E20.filletArc"),sQuery(id+"F0.wireOp",EDGE,"E25.0"),sQuery(id+"F0.wireOp",EDGE,"E25.1"),sQuery(id+"F0.wireOp",EDGE,"E25.2"),sQuery(id+"F0.wireOp",EDGE,"E25.3"),sQuery(id+"F0.wireOp",EDGE,"E25.4"),sQuery(id+"F0.wireOp",EDGE,"E25.5"),sQuery(id+"F0.wireOp",EDGE,"E25.6"),sQuery(id+"F0.wireOp",EDGE,"E25.7")])],"isStart":false});
            extrude(context, id + "F17", {"entities" : qUnion([Q0, Q1, Q2, Q3]), "operationType" : NewBodyOperationType.ADD, "depth" : 25 * mm});
        }
    });
